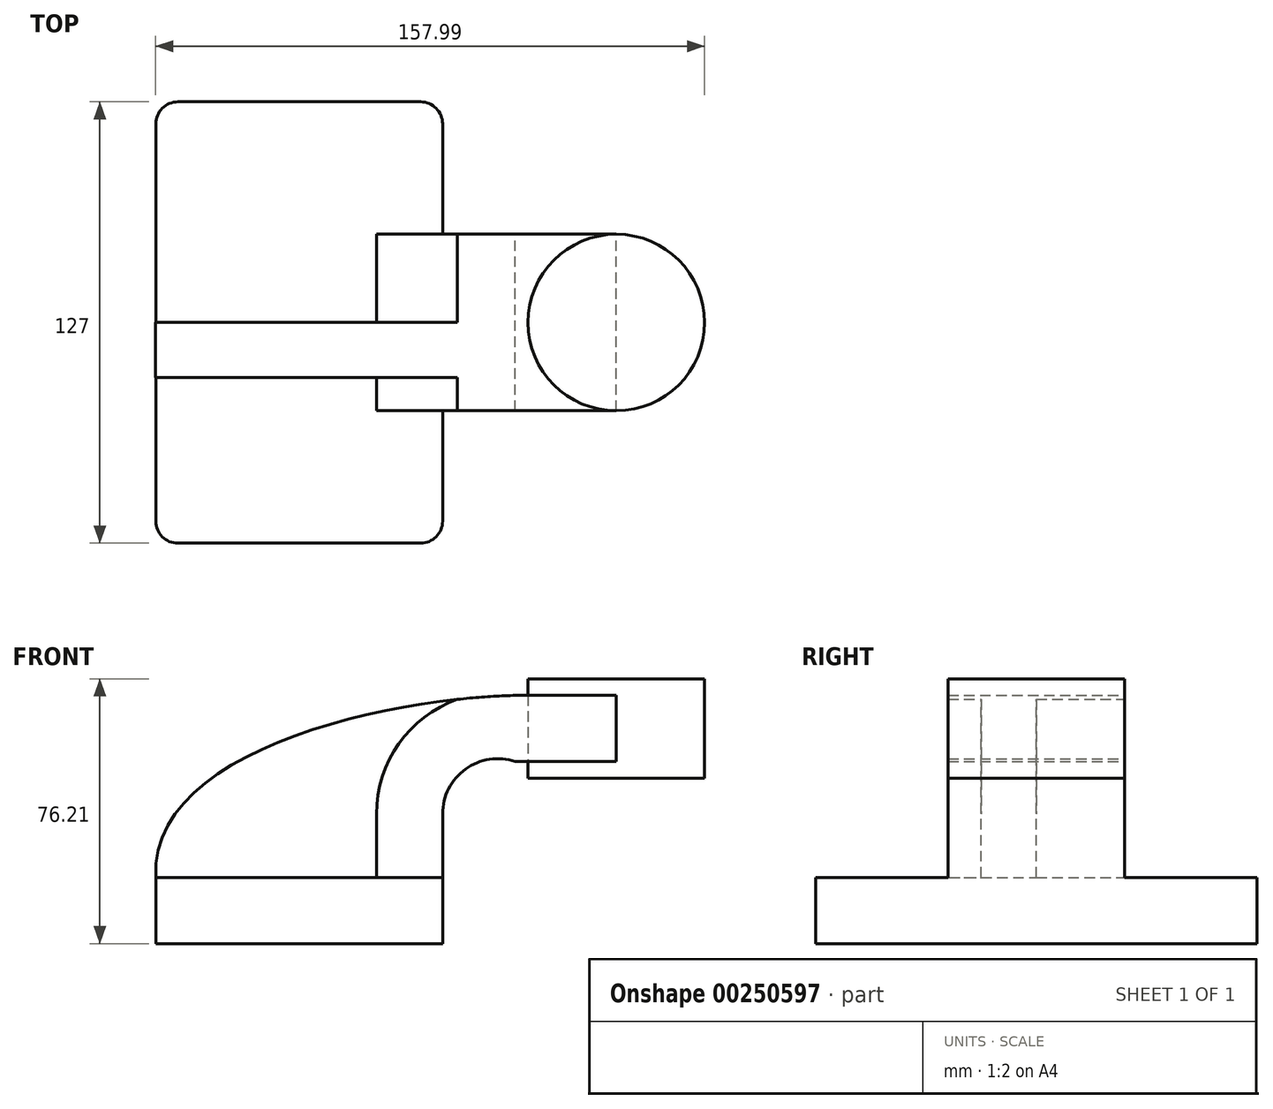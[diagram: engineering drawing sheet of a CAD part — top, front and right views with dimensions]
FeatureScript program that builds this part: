
annotation { "Feature Type Name" : "Feature", "Feature Type Description" : "" }
export const myFeature = defineFeature(function(context is Context, id is Id, definition is map)
    precondition{}
    {
        {
            var Q0;
            Q0=qCreatedBy(makeId("Front.planeOp"),FACE);
            var sketch = newSketch(context, id + "F0", { "sketchPlane" : qUnion([Q0])});
            skLineSegment(sketch, "E0.bottom", {"start": v(41.27, 9.53) * mm, "end": v(-41.28, 9.53) * mm});
            skLineSegment(sketch, "E0.top", {"start": v(41.28, -9.52) * mm, "end": v(-41.27, -9.52) * mm});
            skLineSegment(sketch, "E0.left", {"start": v(41.28, 9.53) * mm, "end": v(41.28, -9.52) * mm});
            skLineSegment(sketch, "E0.right", {"start": v(-41.28, 9.53) * mm, "end": v(-41.27, -9.52) * mm});
            skPoint(sketch, "E0.middle", {"position": v(0, 0) * mm});
            skLineSegment(sketch, "E1.bottom", {"start": v(116.66, 66.68) * mm, "end": v(65.86, 66.68) * mm});
            skLineSegment(sketch, "E1.top", {"start": v(116.66, 38.1) * mm, "end": v(65.86, 38.1) * mm});
            skLineSegment(sketch, "E1.left", {"start": v(116.66, 66.68) * mm, "end": v(116.66, 38.1) * mm});
            skLineSegment(sketch, "E1.right", {"start": v(65.86, 66.68) * mm, "end": v(65.86, 38.1) * mm});
            skPoint(sketch, "E1.middle", {"position": v(91.26, 52.39) * mm});
            skLineSegment(sketch, "E2", {"start": v(41.27, 9.53) * mm, "end": v(41.27, 27.81) * mm});
            skArc(sketch, "E3", {"start": v(41.27, 27.81) * mm, "mid": v(47.86, 40.69) * mm, "end": v(62.16, 42.88) * mm});
            skLineSegment(sketch, "E4", {"start": v(62.16, 42.88) * mm, "end": v(91.26, 42.88) * mm});
            skPoint(sketch, "E4.endSnap0", {"position": v(91.26, 38.1) * mm});
            skLineSegment(sketch, "E5.0", {"start": v(64.63, 61.93) * mm, "end": v(91.26, 61.93) * mm});
            skArc(sketch, "E5.1", {"start": v(22.23, 27.81) * mm, "mid": v(35.26, 55.03) * mm, "end": v(64.63, 61.93) * mm});
            skLineSegment(sketch, "E5.2", {"start": v(22.22, 9.53) * mm, "end": v(22.22, 27.81) * mm});
            skFitSpline(sketch, "E6", {"points": [v(-41.28, 9.53) * mm, v(64.63, 61.93) * mm], "startDerivative": vector(-6.56, 110.16) * mm, "endDerivative": vector(115.09, 0.87) * mm});
            skLineSegment(sketch, "E7", {"start": v(91.26, 61.93) * mm, "end": v(91.26, 42.88) * mm});
            skLineSegment(sketch, "E8", {"start": v(91.26, 38.1) * mm, "end": v(91.26, 66.68) * mm});
            skSolve(sketch);
        }
        {
            var Q0;
            Q0=qCreatedBy(makeId("Front.planeOp"),FACE);
            var sketch = newSketch(context, id + "F1", { "sketchPlane" : qUnion([Q0])});
            skSolve(sketch);
        }
        {
            var Q0;
            Q0=makeQuery(id+"F0.imprint","IMPRINT",FACE,{"disambiguationData":[TD([[makeQuery(id+"F0.imprint","IMPRINT",EDGE,{"derivedFrom":sQuery(id+"F0.wireOp",EDGE,"E0.top")}),-1.0]])]});
            extrude(context, id + "F2", {"entities" : qUnion([Q0]), "endBound" : BoundingType.SYMMETRIC, "depth" : 127 * mm});
        }
        {
            var Q0;
            {var subQ1=sQuery(id+"F0.wireOp",EDGE,"E2");Q0=makeQuery(id+"F0.imprint","IMPRINT",FACE,{"disambiguationData":[TD([[makeQuery(id+"F0.imprint","IMPRINT",EDGE,{"derivedFrom":subQ1}),1.0]])]});}
            var Q1;
            Q1 = qSketchRegion(id + "F1", true);
            var Q2;
            {var subQ0=sQuery(id+"F0.wireOp",EDGE,"E5.0");var subQ1=sQuery(id+"F0.wireOp",EDGE,"E1.right");var subQ2=makeQuery(id+"F0.imprint","INTERSECT",VERTEX,{"derivedFrom":[subQ1,subQ0]});Q2=makeQuery(id+"F0.imprint","IMPRINT",FACE,{"disambiguationData":[TD([[makeQuery(id+"F0.imprint","IMPRINT",EDGE,{"disambiguationData":[TD([[subQ2,-1.0]])],"derivedFrom":subQ1}),1.0]])]});}
            extrude(context, id + "F3", {"entities" : qUnion([Q0, Q1, Q2]), "operationType" : NewBodyOperationType.ADD, "endBound" : BoundingType.SYMMETRIC, "depth" : 50.8 * mm});
        }
        {
            var Q0;
            {var subQ3=sQuery(id+"F0.wireOp",EDGE,"E5.2");Q0=makeQuery(id+"F0.imprint","IMPRINT",FACE,{"disambiguationData":[TD([[makeQuery(id+"F0.imprint","IMPRINT",EDGE,{"derivedFrom":subQ3}),1.0]])]});}
            extrude(context, id + "F4", {"entities" : qUnion([Q0]), "operationType" : NewBodyOperationType.ADD, "depth" : 15.88 * mm});
        }
        {
            var Q0;
            {var subQ4=sQuery(id+"F0.wireOp",EDGE,"E1.left");Q0=makeQuery(id+"F0.imprint","IMPRINT",FACE,{"disambiguationData":[TD([[makeQuery(id+"F0.imprint","IMPRINT",EDGE,{"derivedFrom":subQ4}),-1.0]])]});}
            var Q1;
            Q1=sQuery(id+"F0.wireOp",EDGE,"E8");
            revolve(context, id + "F5", {"entities" : qUnion([Q0]), "axis" : qUnion([Q1]), "revolveType" : RevolveType.FULL});
        }
        {
            var Q0;
            Q0=makeQuery(id+"F2.opExtrude","CAP_EDGE",EDGE,{"disambiguationData":[OSD([sQuery(id+"F0.wireOp",EDGE,"E0.left")])],"isStart":false});
            var Q1;
            Q1=makeQuery(id+"F2.opExtrude","CAP_EDGE",EDGE,{"disambiguationData":[OSD([sQuery(id+"F0.wireOp",EDGE,"E0.right")])],"isStart":false});
            var Q2;
            Q2=makeQuery(id+"F2.opExtrude","CAP_EDGE",EDGE,{"disambiguationData":[OSD([sQuery(id+"F0.wireOp",EDGE,"E0.right")])],"isStart":true});
            var Q3;
            Q3=makeQuery(id+"F2.opExtrude","CAP_EDGE",EDGE,{"disambiguationData":[OSD([sQuery(id+"F0.wireOp",EDGE,"E0.left")])],"isStart":true});
            fillet(context, id + "F6", {"entities" : qUnion([Q0, Q1, Q2, Q3]), "radius" : 6.35 * mm, "tangentPropagation" : true, "allowEdgeOverflow" : false});
        }
    });
